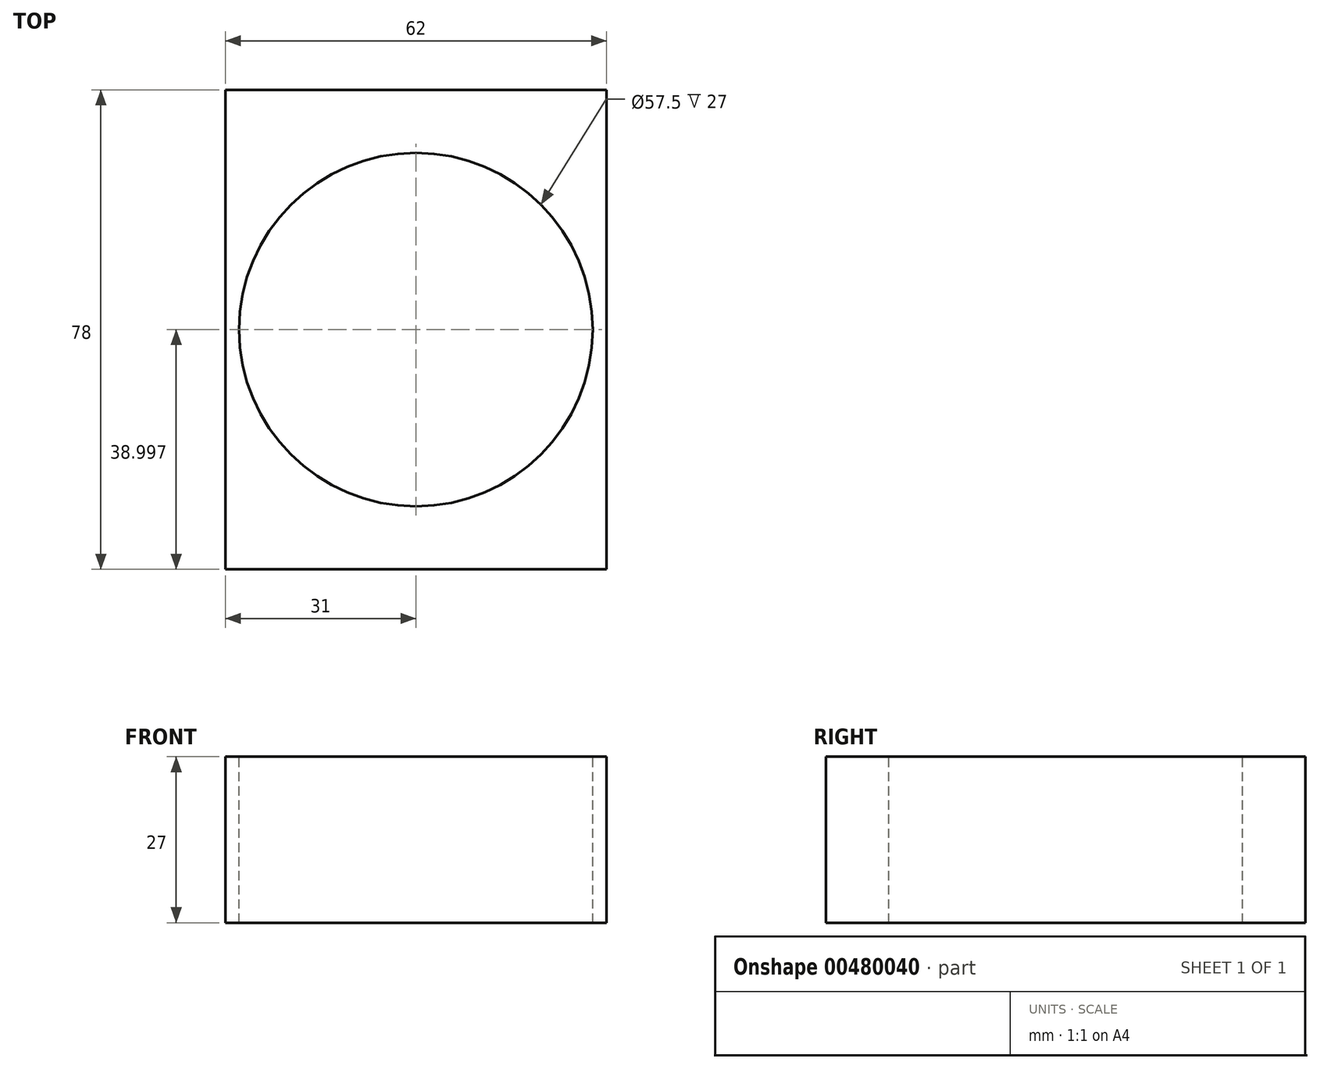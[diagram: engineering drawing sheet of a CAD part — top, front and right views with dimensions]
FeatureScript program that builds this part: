
annotation { "Feature Type Name" : "Feature", "Feature Type Description" : "" }
export const myFeature = defineFeature(function(context is Context, id is Id, definition is map)
    precondition{}
    {
        {
            var Q0;
            Q0=qCreatedBy(makeId("Top.planeOp"),FACE);
            var sketch = newSketch(context, id + "F0", { "sketchPlane" : qUnion([Q0])});
            skLineSegment(sketch, "E0.bottom", {"start": v(-26.4, 55.84) * mm, "end": v(35.6, 55.84) * mm});
            skLineSegment(sketch, "E0.top", {"start": v(-26.4, -22.16) * mm, "end": v(35.6, -22.16) * mm});
            skLineSegment(sketch, "E0.left", {"start": v(-26.4, 55.84) * mm, "end": v(-26.4, -22.16) * mm});
            skLineSegment(sketch, "E0.right", {"start": v(35.6, 55.84) * mm, "end": v(35.6, -22.16) * mm});
            skLineSegment(sketch, "E1", {"start": v(-26.4, -22.16) * mm, "end": v(35.6, 55.84) * mm, "construction": true});
            skSolve(sketch);
        }
        {
            var Q0;
            Q0=qSketchRegion(id+"F0",true);
            extrude(context, id + "F1", {"entities" : qUnion([Q0]), "depth" : 27 * mm});
        }
        {
            var Q0;
            Q0=makeQuery(id+"F1.opExtrude","CAP_FACE",FACE,{"disambiguationData":[OSD([sQuery(id+"F0.wireOp",EDGE,"E0.bottom"),sQuery(id+"F0.wireOp",EDGE,"E0.top"),sQuery(id+"F0.wireOp",EDGE,"E0.left"),sQuery(id+"F0.wireOp",EDGE,"E0.right")])],"isStart":false});
            var sketch = newSketch(context, id + "F2", { "sketchPlane" : qUnion([Q0])});
            skCircle(sketch, "E2", {"center": v(4.6, 16.84) * mm, "radius": 28.75 * mm});
            skSolve(sketch);
        }
        {
            var Q0;
            Q0=qSketchRegion(id+"F2",true);
            extrude(context, id + "F3", {"entities" : qUnion([Q0]), "operationType" : NewBodyOperationType.REMOVE, "oppositeDirection" : true, "depth" : 27 * mm});
        }
    });
